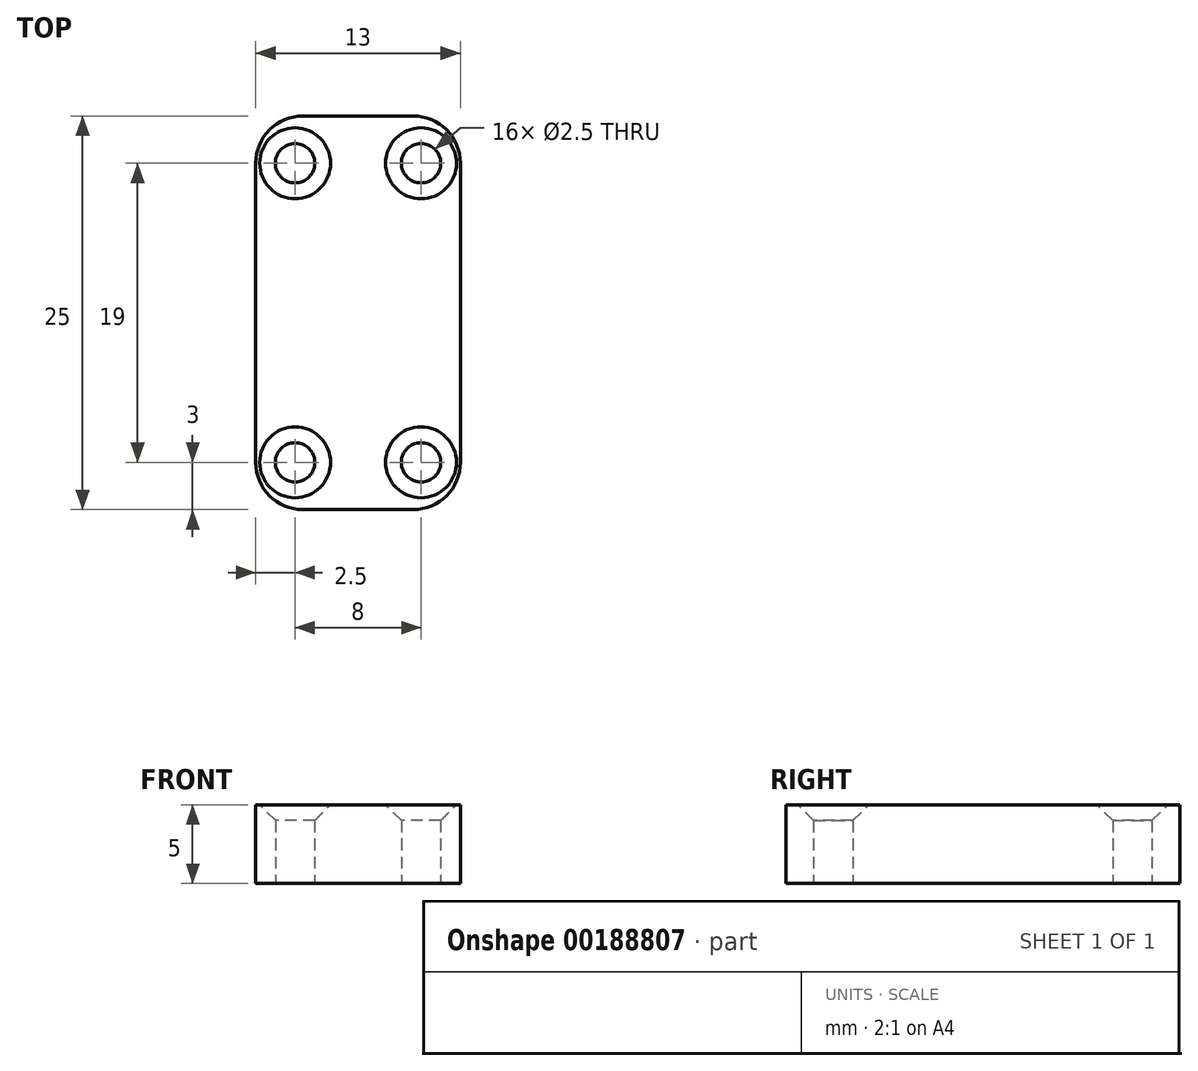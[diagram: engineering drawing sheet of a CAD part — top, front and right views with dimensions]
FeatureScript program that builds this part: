
annotation { "Feature Type Name" : "Feature", "Feature Type Description" : "" }
export const myFeature = defineFeature(function(context is Context, id is Id, definition is map)
    precondition{}
    {
        {
            var Q0;
            Q0=qCreatedBy(makeId("Top.planeOp"),FACE);
            var sketch = newSketch(context, id + "F0", { "sketchPlane" : qUnion([Q0])});
            skLineSegment(sketch, "E0.bottom", {"start": v(6.5, 12.5) * mm, "end": v(-6.5, 12.5) * mm});
            skLineSegment(sketch, "E0.top", {"start": v(6.5, -12.5) * mm, "end": v(-6.5, -12.5) * mm});
            skLineSegment(sketch, "E0.left", {"start": v(6.5, 12.5) * mm, "end": v(6.5, -12.5) * mm});
            skLineSegment(sketch, "E0.right", {"start": v(-6.5, 12.5) * mm, "end": v(-6.5, -12.5) * mm});
            skPoint(sketch, "E0.middle", {"position": v(0, 0) * mm});
            skLineSegment(sketch, "E1", {"start": v(-6.5, 9.5) * mm, "end": v(6.5, 9.5) * mm, "construction": true});
            skLineSegment(sketch, "E2", {"start": v(-6.5, -9.5) * mm, "end": v(6.5, -9.5) * mm, "construction": true});
            skLineSegment(sketch, "E3", {"start": v(-4, -12.5) * mm, "end": v(-4, 13.45) * mm, "construction": true});
            skCircle(sketch, "E4", {"center": v(-4, -9.5) * mm, "radius": 1.25 * mm});
            skCircle(sketch, "E5", {"center": v(-4, 9.5) * mm, "radius": 1.25 * mm});
            skCircle(sketch, "E6", {"center": v(4, 9.5) * mm, "radius": 1.25 * mm});
            skCircle(sketch, "E7", {"center": v(4, -9.5) * mm, "radius": 1.25 * mm});
            skSolve(sketch);
        }
        {
            var Q0;
            Q0=makeQuery(id+"F0.imprint","IMPRINT",FACE,{"disambiguationData":[TD([[makeQuery(id+"F0.imprint","IMPRINT",EDGE,{"derivedFrom":sQuery(id+"F0.wireOp",EDGE,"E0.bottom")}),1.0]])]});
            extrude(context, id + "F1", {"entities" : qUnion([Q0]), "depth" : 5 * mm});
        }
        {
            var Q0;
            Q0=makeQuery(id+"F1.opExtrude","SWEPT_EDGE",EDGE,{"disambiguationData":[OSD([sQuery(id+"F0.wireOp",EDGE,"E0.top"),sQuery(id+"F0.wireOp",EDGE,"E0.right")])]});
            var Q1;
            Q1=makeQuery(id+"F1.opExtrude","SWEPT_EDGE",EDGE,{"disambiguationData":[OSD([sQuery(id+"F0.wireOp",EDGE,"E0.top"),sQuery(id+"F0.wireOp",EDGE,"E0.left")])]});
            var Q2;
            Q2=makeQuery(id+"F1.opExtrude","SWEPT_EDGE",EDGE,{"disambiguationData":[OSD([sQuery(id+"F0.wireOp",EDGE,"E0.bottom"),sQuery(id+"F0.wireOp",EDGE,"E0.left")])]});
            var Q3;
            Q3=makeQuery(id+"F1.opExtrude","SWEPT_EDGE",EDGE,{"disambiguationData":[OSD([sQuery(id+"F0.wireOp",EDGE,"E0.bottom"),sQuery(id+"F0.wireOp",EDGE,"E0.right")])]});
            fillet(context, id + "F2", {"entities" : qUnion([Q0, Q1, Q2, Q3]), "radius" : 3 * mm, "tangentPropagation" : true, "allowEdgeOverflow" : false});
        }
        {
            var Q0;
            Q0=makeQuery(id+"F1.opExtrude","CAP_EDGE",EDGE,{"disambiguationData":[OSD([sQuery(id+"F0.wireOp",EDGE,"E5")])],"isStart":false});
            var Q1;
            Q1=makeQuery(id+"F1.opExtrude","CAP_EDGE",EDGE,{"disambiguationData":[OSD([sQuery(id+"F0.wireOp",EDGE,"E6")])],"isStart":false});
            var Q2;
            Q2=makeQuery(id+"F1.opExtrude","CAP_EDGE",EDGE,{"disambiguationData":[OSD([sQuery(id+"F0.wireOp",EDGE,"E7")])],"isStart":false});
            var Q3;
            Q3=makeQuery(id+"F1.opExtrude","CAP_EDGE",EDGE,{"disambiguationData":[OSD([sQuery(id+"F0.wireOp",EDGE,"E4")])],"isStart":false});
            chamfer(context, id + "F3", {"entities" : qUnion([Q0, Q1, Q2, Q3]), "width" : 1 * mm, "tangentPropagation" : true});
        }
    });
